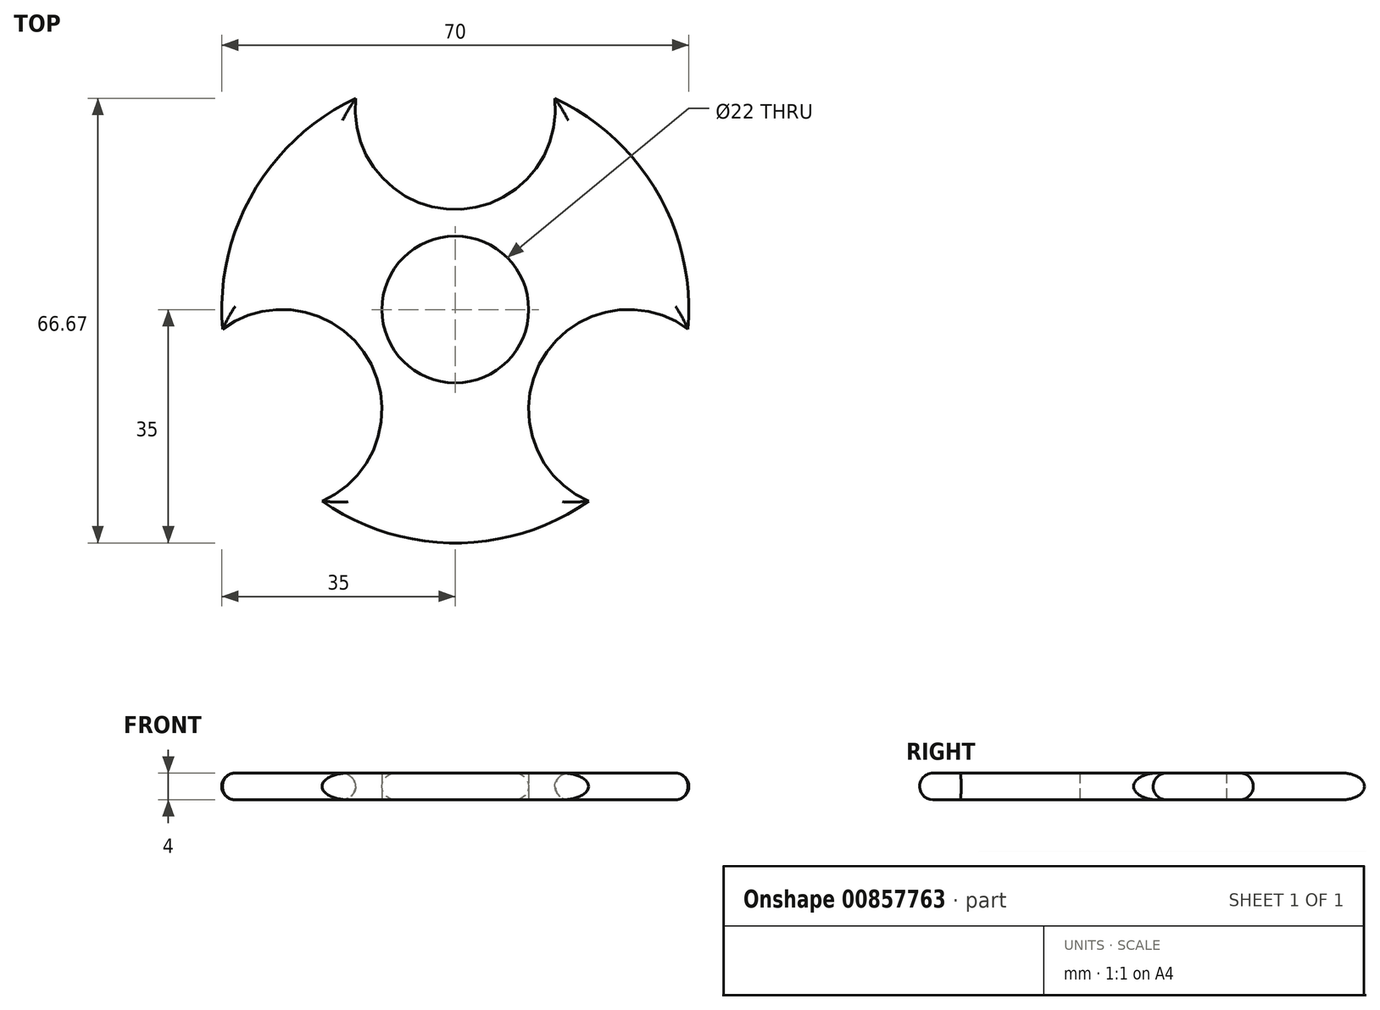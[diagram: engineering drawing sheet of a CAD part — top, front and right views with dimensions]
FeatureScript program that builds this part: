
annotation { "Feature Type Name" : "Feature", "Feature Type Description" : "" }
export const myFeature = defineFeature(function(context is Context, id is Id, definition is map)
    precondition{}
    {
        {
            var Q0;
            Q0=qCreatedBy(makeId("Top.planeOp"),FACE);
            var sketch = newSketch(context, id + "F0", { "sketchPlane" : qUnion([Q0])});
            skCircle(sketch, "E0", {"center": v(0, 0) * mm, "radius": 11 * mm});
            skArc(sketch, "E1", {"start": v(-14.9, 31.67) * mm, "mid": v(0, 15) * mm, "end": v(14.9, 31.67) * mm});
            skArc(sketch, "E2", {"start": v(34.88, -2.92) * mm, "mid": v(30.31, 17.5) * mm, "end": v(14.9, 31.67) * mm});
            skArc(sketch, "E3.1.0", {"start": v(-19.97, -28.74) * mm, "mid": v(-13, -7.5) * mm, "end": v(-34.88, -2.92) * mm});
            skArc(sketch, "E3.2.0", {"start": v(34.88, -2.92) * mm, "mid": v(13, -7.5) * mm, "end": v(19.97, -28.74) * mm});
            skArc(sketch, "E4.trimOffspring", {"start": v(-19.97, -28.74) * mm, "mid": v(0, -35) * mm, "end": v(19.97, -28.74) * mm});
            skArc(sketch, "E5.trimOffspring", {"start": v(-14.9, 31.67) * mm, "mid": v(-30.31, 17.5) * mm, "end": v(-34.88, -2.92) * mm});
            skSolve(sketch);
        }
        {
            var Q0;
            Q0=makeQuery(id+"F0.imprint","IMPRINT",FACE,{"disambiguationData":[TD([[makeQuery(id+"F0.imprint","IMPRINT",EDGE,{"derivedFrom":sQuery(id+"F0.wireOp",EDGE,"E0")}),-1.0]])]});
            extrude(context, id + "F1", {"entities" : qUnion([Q0]), "endBound" : BoundingType.SYMMETRIC, "depth" : 4 * mm, "offsetDistance" : 25 * mm});
        }
        {
            var Q0;
            Q0=makeQuery(id+"F1.opExtrude","CAP_EDGE",EDGE,{"disambiguationData":[OSD([sQuery(id+"F0.wireOp",EDGE,"E4.trimOffspring")])],"isStart":false});
            var Q1;
            Q1=makeQuery(id+"F1.opExtrude","CAP_EDGE",EDGE,{"disambiguationData":[OSD([sQuery(id+"F0.wireOp",EDGE,"E3.1.0")])],"isStart":false});
            var Q2;
            Q2=makeQuery(id+"F1.opExtrude","CAP_EDGE",EDGE,{"disambiguationData":[OSD([sQuery(id+"F0.wireOp",EDGE,"E2")])],"isStart":false});
            var Q3;
            Q3=makeQuery(id+"F1.opExtrude","CAP_EDGE",EDGE,{"disambiguationData":[OSD([sQuery(id+"F0.wireOp",EDGE,"E3.1.0")])],"isStart":true});
            var Q4;
            Q4=makeQuery(id+"F1.opExtrude","CAP_EDGE",EDGE,{"disambiguationData":[OSD([sQuery(id+"F0.wireOp",EDGE,"E1")])],"isStart":true});
            var Q5;
            Q5=makeQuery(id+"F1.opExtrude","CAP_EDGE",EDGE,{"disambiguationData":[OSD([sQuery(id+"F0.wireOp",EDGE,"E1")])],"isStart":false});
            var Q6;
            Q6=makeQuery(id+"F1.opExtrude","CAP_EDGE",EDGE,{"disambiguationData":[OSD([sQuery(id+"F0.wireOp",EDGE,"E5.trimOffspring")])],"isStart":true});
            var Q7;
            Q7=makeQuery(id+"F1.opExtrude","CAP_EDGE",EDGE,{"disambiguationData":[OSD([sQuery(id+"F0.wireOp",EDGE,"E5.trimOffspring")])],"isStart":false});
            var Q8;
            Q8=makeQuery(id+"F1.opExtrude","CAP_EDGE",EDGE,{"disambiguationData":[OSD([sQuery(id+"F0.wireOp",EDGE,"E2")])],"isStart":true});
            var Q9;
            Q9=makeQuery(id+"F1.opExtrude","CAP_EDGE",EDGE,{"disambiguationData":[OSD([sQuery(id+"F0.wireOp",EDGE,"E3.2.0")])],"isStart":false});
            var Q10;
            Q10=makeQuery(id+"F1.opExtrude","CAP_EDGE",EDGE,{"disambiguationData":[OSD([sQuery(id+"F0.wireOp",EDGE,"E3.2.0")])],"isStart":true});
            var Q11;
            Q11=makeQuery(id+"F1.opExtrude","CAP_EDGE",EDGE,{"disambiguationData":[OSD([sQuery(id+"F0.wireOp",EDGE,"E4.trimOffspring")])],"isStart":true});
            fillet(context, id + "F2", {"entities" : qUnion([Q0, Q1, Q2, Q3, Q4, Q5, Q6, Q7, Q8, Q9, Q10, Q11]), "radius" : 2 * mm, "tangentPropagation" : true, "allowEdgeOverflow" : false});
        }
    });
